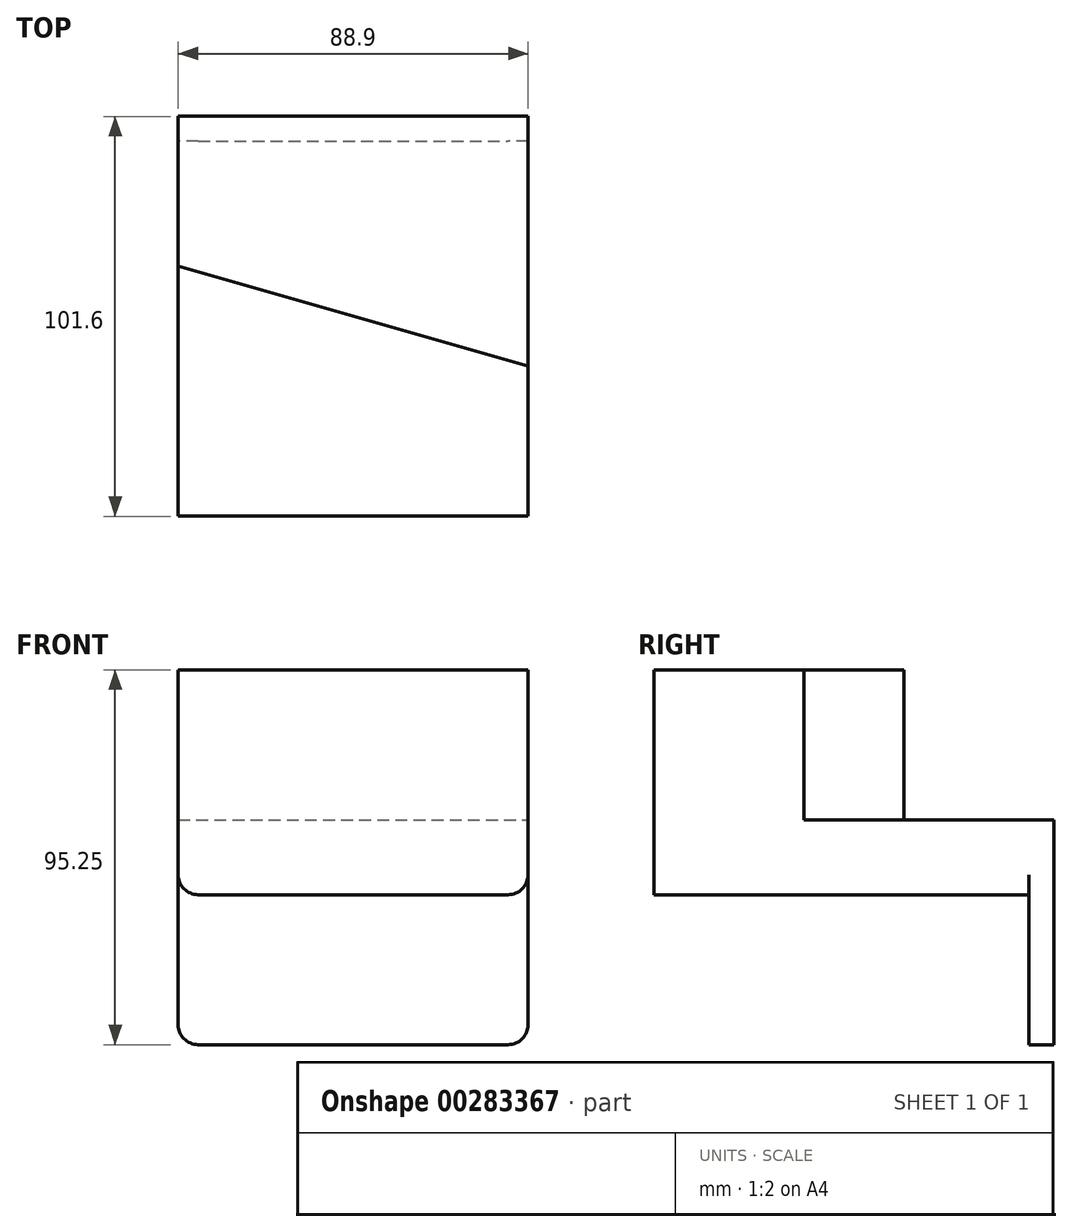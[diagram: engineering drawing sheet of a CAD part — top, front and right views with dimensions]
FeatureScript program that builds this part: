
annotation { "Feature Type Name" : "Feature", "Feature Type Description" : "" }
export const myFeature = defineFeature(function(context is Context, id is Id, definition is map)
    precondition{}
    {
        {
            var Q0;
            Q0=qCreatedBy(makeId("Top.planeOp"),FACE);
            var sketch = newSketch(context, id + "F0", { "sketchPlane" : qUnion([Q0])});
            skLineSegment(sketch, "E0", {"start": v(-31.98, -40.3) * mm, "end": v(56.92, -40.3) * mm});
            skLineSegment(sketch, "E1", {"start": v(56.92, -40.3) * mm, "end": v(56.92, -2.2) * mm});
            skLineSegment(sketch, "E2", {"start": v(-31.98, -40.3) * mm, "end": v(-31.98, 23.2) * mm});
            skLineSegment(sketch, "E3", {"start": v(-31.98, 23.2) * mm, "end": v(56.92, -2.2) * mm});
            skSolve(sketch);
        }
        {
            var Q0;
            Q0=qSketchRegion(id+"F0",true);
            extrude(context, id + "F1", {"entities" : qUnion([Q0]), "depth" : 38.1 * mm});
        }
        {
            var Q0;
            Q0=makeQuery(id+"F1.opExtrude","CAP_FACE",FACE,{"disambiguationData":[OSD([sQuery(id+"F0.wireOp",EDGE,"E0"),sQuery(id+"F0.wireOp",EDGE,"E1"),sQuery(id+"F0.wireOp",EDGE,"E2"),sQuery(id+"F0.wireOp",EDGE,"E3")])],"isStart":false});
            var sketch = newSketch(context, id + "F2", { "sketchPlane" : qUnion([Q0])});
            skLineSegment(sketch, "E4.bottom", {"start": v(-31.98, -40.3) * mm, "end": v(56.92, -40.3) * mm});
            skLineSegment(sketch, "E4.top", {"start": v(-31.98, 61.3) * mm, "end": v(56.92, 61.3) * mm});
            skLineSegment(sketch, "E4.left", {"start": v(-31.98, -40.3) * mm, "end": v(-31.98, 61.3) * mm});
            skLineSegment(sketch, "E4.right", {"start": v(56.92, -40.3) * mm, "end": v(56.92, 61.3) * mm});
            skSolve(sketch);
        }
        {
            var Q0;
            Q0=qSketchRegion(id+"F2",true);
            extrude(context, id + "F3", {"entities" : qUnion([Q0]), "operationType" : NewBodyOperationType.ADD, "depth" : 19.05 * mm});
        }
        {
            var Q0;
            Q0=makeQuery(id+"F3.opExtrude","CAP_FACE",FACE,{"disambiguationData":[OSD([sQuery(id+"F2.wireOp",EDGE,"E4.bottom"),sQuery(id+"F2.wireOp",EDGE,"E4.top"),sQuery(id+"F2.wireOp",EDGE,"E4.left"),sQuery(id+"F2.wireOp",EDGE,"E4.right")])],"isStart":false});
            var sketch = newSketch(context, id + "F4", { "sketchPlane" : qUnion([Q0])});
            skLineSegment(sketch, "E5.bottom", {"start": v(-31.98, 61.3) * mm, "end": v(56.92, 61.3) * mm});
            skLineSegment(sketch, "E5.top", {"start": v(-31.98, 54.95) * mm, "end": v(56.92, 54.95) * mm});
            skLineSegment(sketch, "E5.left", {"start": v(-31.98, 61.3) * mm, "end": v(-31.98, 54.95) * mm});
            skLineSegment(sketch, "E5.right", {"start": v(56.92, 61.3) * mm, "end": v(56.92, 54.95) * mm});
            skSolve(sketch);
        }
        {
            var Q0;
            Q0=qSketchRegion(id+"F4",true);
            extrude(context, id + "F5", {"entities" : qUnion([Q0]), "operationType" : NewBodyOperationType.ADD, "depth" : 38.1 * mm});
        }
        {
            var Q0;
            Q0=makeQuery(id+"F1.opExtrude","SWEPT_BODY",BODY,{"disambiguationData":[OSD([sQuery(id+"F0.wireOp",EDGE,"E0"),sQuery(id+"F0.wireOp",EDGE,"E1"),sQuery(id+"F0.wireOp",EDGE,"E2"),sQuery(id+"F0.wireOp",EDGE,"E3")])]});
            var Q1;
            Q1=qCreatedBy(makeId("Top.planeOp"),FACE);
            mirror(context, id + "F6", {"entities" : qUnion([Q0]), "mirrorPlane" : qUnion([Q1])});
        }
        {
            var Q0;
            Q0=makeQuery(id+"F1.opExtrude","SWEPT_BODY",BODY,{"disambiguationData":[OSD([sQuery(id+"F0.wireOp",EDGE,"E0"),sQuery(id+"F0.wireOp",EDGE,"E1"),sQuery(id+"F0.wireOp",EDGE,"E2"),sQuery(id+"F0.wireOp",EDGE,"E3")])]});
            deleteBodies(context, id + "F7", {"entities" : qUnion([Q0])});
        }
        {
            var Q0;
            Q0=makeQuery(id+"F6.opPattern","COPY",EDGE,{"derivedFrom":makeQuery(id+"F3.opExtrude","CAP_EDGE",EDGE,{"disambiguationData":[OSD([sQuery(id+"F2.wireOp",EDGE,"E4.right")])],"isStart":false}),"instanceName":"1"});
            var Q1;
            Q1=makeQuery(id+"F6.opPattern","COPY",EDGE,{"derivedFrom":makeQuery(id+"F3.opExtrude","CAP_EDGE",EDGE,{"disambiguationData":[OSD([sQuery(id+"F2.wireOp",EDGE,"E4.left")])],"isStart":false}),"instanceName":"1"});
            var Q2;
            Q2=makeQuery(id+"F6.opPattern","COPY",EDGE,{"derivedFrom":makeQuery(id+"F5.opExtrude","CAP_EDGE",EDGE,{"disambiguationData":[OSD([sQuery(id+"F4.wireOp",EDGE,"E5.right")])],"isStart":false}),"instanceName":"1"});
            var Q3;
            Q3=makeQuery(id+"F6.opPattern","COPY",EDGE,{"derivedFrom":makeQuery(id+"F5.opExtrude","CAP_EDGE",EDGE,{"disambiguationData":[OSD([sQuery(id+"F4.wireOp",EDGE,"E5.left")])],"isStart":false}),"instanceName":"1"});
            fillet(context, id + "F8", {"entities" : qUnion([Q0, Q1, Q2, Q3]), "radius" : 5.08 * mm, "tangentPropagation" : true, "allowEdgeOverflow" : false});
        }
    });
